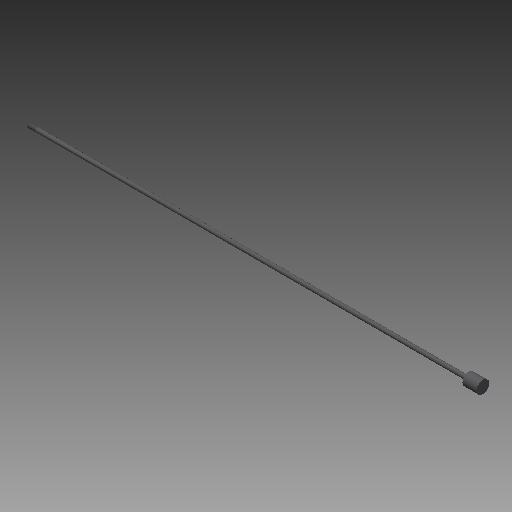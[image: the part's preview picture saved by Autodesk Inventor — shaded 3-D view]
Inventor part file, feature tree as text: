
AUTODESK INVENTOR PART (.ipt)
format: ipt  version: 2018 (Build 220112000, 112)  size: 137,216 bytes
history: native  units: in
note: dims shown in document units (in); Inventor stores cm internally (conversion verified against a paired STEP export)
features: other x70, revolve x3, sketch x3, thread x1
ambient origin geometry x8: Origin, YZ Plane, XZ Plane, XY Plane, X Axis, Y Axis, Z Axis, Center Point
bodies: Solid1 (feature_tree)
feature tree (77):
  revolve  "Revolution1"  Angle=360.0deg
  revolve  "Revolution2"  Angle=360.0deg
  thread  "Thread1"  [1 undecoded]
  revolve  "Revolution3"  [1 undecoded]
  other  "dia1_XY"
  other  "dia1_YZ"
  other  "dia1_ZX"
  other  "dia1_X"
  other  "dia1_Y"
  other  "dia1_Z"
  other  "dia1_Center"
  other  "dia12_XY"
  other  "dia12_YZ"
  other  "dia12_ZX"
  other  "dia12_X"
  other  "dia12_Y"
  other  "dia12_Z"
  other  "dia12_Center"
  other  "dia2_XY"
  other  "dia2_YZ"
  other  "dia2_ZX"
  other  "dia2_X"
  other  "dia2_Y"
  other  "dia2_Z"
  other  "dia2_Center"
  other  "dia22_XY"
  other  "dia22_YZ"
  other  "dia22_ZX"
  other  "dia22_X"
  other  "dia22_Y"
  other  "dia22_Z"
  other  "dia22_Center"
  other  "rl1_XY"
  other  "rl1_YZ"
  other  "rl1_ZX"
  other  "rl1_X"
  other  "rl1_Y"
  other  "rl1_Z"
  other  "rl1_Center"
  other  "rl2_XY"
  other  "rl2_YZ"
  other  "rl2_ZX"
  other  "rl2_X"
  other  "rl2_Y"
  other  "rl2_Z"
  other  "rl2_Center"
  other  "rod_cp_XY"
  other  "rod_cp_YZ"
  other  "rod_cp_ZX"
  other  "rod_cp_X"
  other  "rod_cp_Y"
  other  "rod_cp_Z"
  other  "rod_cp_Center"
  other  "thd1_XY"
  other  "thd1_YZ"
  other  "thd1_ZX"
  other  "thd1_X"
  other  "thd1_Y"
  other  "thd1_Z"
  other  "thd1_Center"
  other  "thd2_XY"
  other  "thd2_YZ"
  other  "thd2_ZX"
  other  "thd2_X"
  other  "thd2_Y"
  other  "thd2_Z"
  other  "thd2_Center"
  other  "to_rod_clevis_XY"
  other  "to_rod_clevis_YZ"
  other  "to_rod_clevis_ZX"
  other  "to_rod_clevis_X"
  other  "to_rod_clevis_Y"
  other  "to_rod_clevis_Z"
  other  "to_rod_clevis_Center"
  sketch  "Sketch_1"  dims[d0=360.0deg d1=360.0deg]
  sketch  "Sketch_3"  dims[d2=0.4787in d3=0.0in d4=360.0deg d5=0.0in d6=0.0in d7=0.0in]
  sketch  "Sketch_30"
note: 2 required parameter values undecoded (feature->parameter linkage not recoverable at this tier; creation-order binding heuristic only, values carry confidence <= 0.55)
